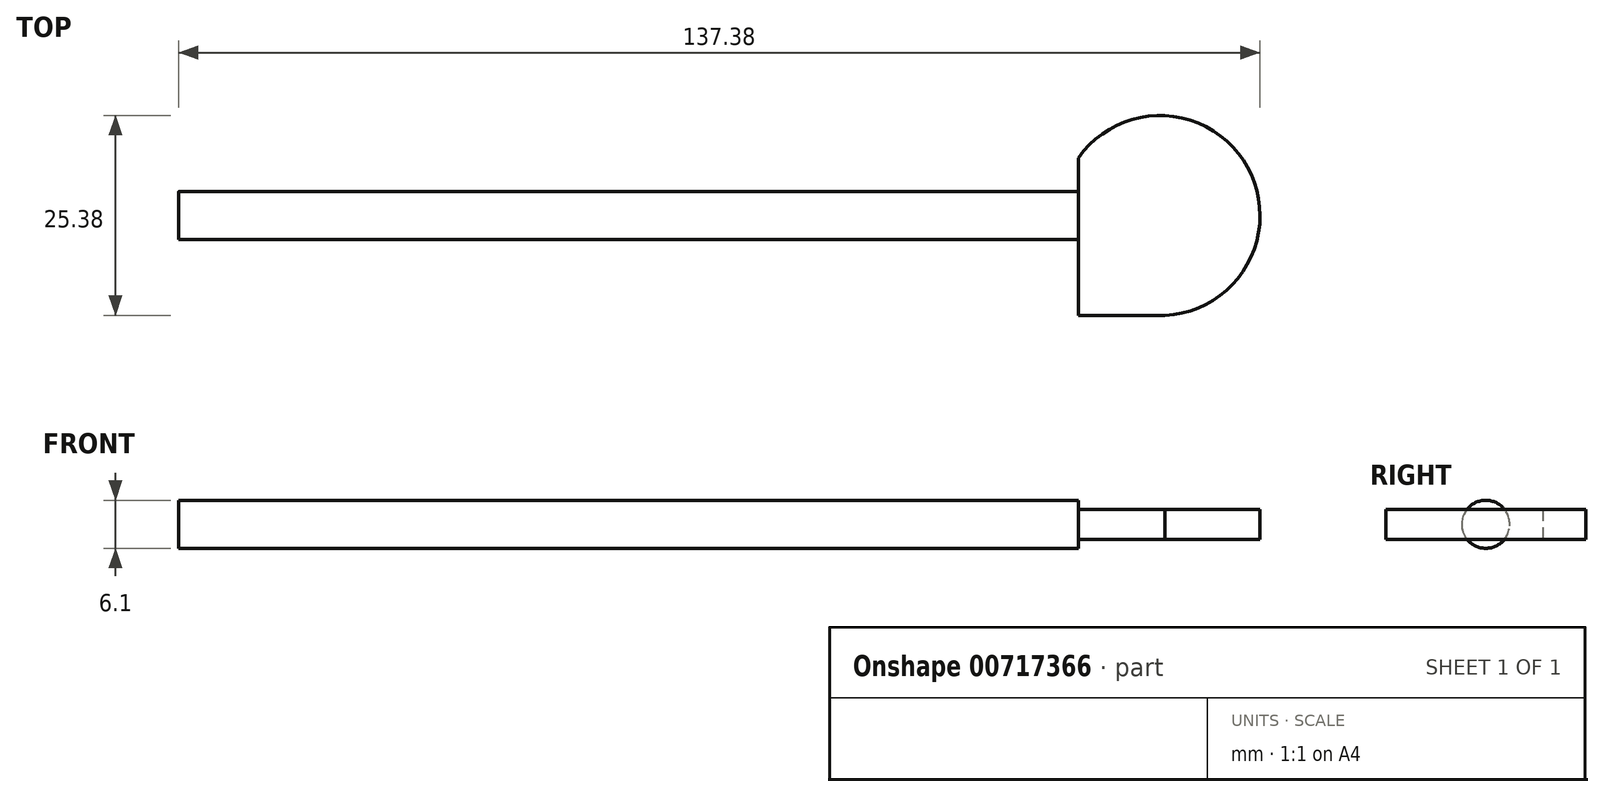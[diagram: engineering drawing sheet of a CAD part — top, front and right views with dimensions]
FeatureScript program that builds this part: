
annotation { "Feature Type Name" : "Feature", "Feature Type Description" : "" }
export const myFeature = defineFeature(function(context is Context, id is Id, definition is map)
    precondition{}
    {
        {
            var Q0;
            Q0=qCreatedBy(makeId("Right.planeOp"),FACE);
            var sketch = newSketch(context, id + "F0", { "sketchPlane" : qUnion([Q0])});
            skCircle(sketch, "E0", {"center": v(0, 0) * mm, "radius": 3.05 * mm});
            skSolve(sketch);
        }
        {
            var Q0;
            Q0=makeQuery(id+"F0.imprint","IMPRINT",FACE,{"disambiguationData":[TD([[makeQuery(id+"F0.imprint","IMPRINT",EDGE,{"derivedFrom":sQuery(id+"F0.wireOp",EDGE,"E0")}),1.0]])]});
            extrude(context, id + "F1", {"entities" : qUnion([Q0]), "depth" : 114.3 * mm, "offsetDistance" : 25.4 * mm});
        }
        {
            var Q0;
            Q0=makeQuery(id+"F1.opExtrude","CAP_FACE",FACE,{"disambiguationData":[OSD([sQuery(id+"F0.wireOp",EDGE,"E0")])],"isStart":false});
            var sketch = newSketch(context, id + "F2", { "sketchPlane" : qUnion([Q0])});
            skLineSegment(sketch, "E1", {"start": v(-0.77, 2.95) * mm, "end": v(0.8, -2.94) * mm, "construction": true});
            skLineSegment(sketch, "E2", {"start": v(-2.81, -1.18) * mm, "end": v(2.81, 1.18) * mm, "construction": true});
            skLineSegment(sketch, "E3.bottom", {"start": v(12.72, -1.9) * mm, "end": v(-12.68, -1.9) * mm});
            skLineSegment(sketch, "E3.top", {"start": v(12.72, 1.91) * mm, "end": v(-12.68, 1.91) * mm});
            skLineSegment(sketch, "E3.left", {"start": v(12.72, -1.9) * mm, "end": v(12.72, 1.91) * mm});
            skLineSegment(sketch, "E3.right", {"start": v(-12.68, -1.9) * mm, "end": v(-12.68, 1.91) * mm});
            skPoint(sketch, "E3.middle", {"position": v(0.02, 0) * mm});
            skSolve(sketch);
        }
        {
            var Q0;
            {var subQ0=sQuery(id+"F2.wireOp",EDGE,"E3.right");Q0=makeQuery(id+"F2.imprint","IMPRINT",FACE,{"disambiguationData":[TD([[makeQuery(id+"F2.imprint","IMPRINT",EDGE,{"derivedFrom":subQ0}),-1.0]])]});}
            var Q1;
            {var subQ0=sQuery(id+"F2.wireOp",EDGE,"E3.bottom");var subQ1=makeQuery(id+"F1.opExtrude","CAP_EDGE",EDGE,{"disambiguationData":[OSD([sQuery(id+"F0.wireOp",EDGE,"E0")])],"isStart":false});var subQ2=makeQuery(id+"F2.imprint","INTERSECT",VERTEX,{"disambiguationData":[OD(0.0)],"derivedFrom":[subQ1,subQ0]});Q1=makeQuery(id+"F2.imprint","IMPRINT",FACE,{"disambiguationData":[TD([[makeQuery(id+"F2.imprint","IMPRINT",EDGE,{"disambiguationData":[TD([[subQ2,-1.0]])],"derivedFrom":subQ0}),-1.0]])]});}
            var Q2;
            {var subQ0=sQuery(id+"F2.wireOp",EDGE,"E3.left");Q2=makeQuery(id+"F2.imprint","IMPRINT",FACE,{"disambiguationData":[TD([[makeQuery(id+"F2.imprint","IMPRINT",EDGE,{"derivedFrom":subQ0}),1.0]])]});}
            extrude(context, id + "F3", {"entities" : qUnion([Q0, Q1, Q2]), "operationType" : NewBodyOperationType.ADD, "depth" : 25.4 * mm, "offsetDistance" : 25.4 * mm});
        }
        {
            var Q0;
            Q0=makeQuery(id+"F3.opExtrude","SWEPT_FACE",FACE,{"disambiguationData":[OSD([sQuery(id+"F2.wireOp",EDGE,"E3.top")])]});
            var sketch = newSketch(context, id + "F4", { "sketchPlane" : qUnion([Q0])});
            skCircle(sketch, "E4", {"center": v(124.68, 0) * mm, "radius": 12.7 * mm});
            skSolve(sketch);
        }
        {
            var Q0;
            {var subQ0=sQuery(id+"F2.wireOp",EDGE,"E3.top");var subQ1=makeQuery(id+"F3.opExtrude","CAP_EDGE",EDGE,{"disambiguationData":[OSD([subQ0])],"isStart":false});Q0=makeQuery(id+"F4.imprint","IMPRINT",FACE,{"disambiguationData":[TD([[makeQuery(id+"F4.imprint","IMPRINT",EDGE,{"derivedFrom":subQ1}),-1.0]])]});}
            var Q1;
            {var subQ0=sQuery(id+"F4.wireOp",EDGE,"E4");var subQ1=sQuery(id+"F2.wireOp",EDGE,"E3.top");var subQ3=sQuery(id+"F2.wireOp",EDGE,"E3.right");var subQ8=makeQuery(id+"F3.opExtrude","SWEPT_EDGE",EDGE,{"disambiguationData":[OSD([subQ1,subQ3])]});var subQ9=makeQuery(id+"F4.imprint","INTERSECT",VERTEX,{"disambiguationData":[OD(0.0)],"derivedFrom":[subQ8,subQ0]});Q1=makeQuery(id+"F4.imprint","IMPRINT",FACE,{"disambiguationData":[TD([[makeQuery(id+"F4.imprint","IMPRINT",EDGE,{"disambiguationData":[TD([[subQ9,1.0]])],"derivedFrom":subQ0}),-1.0]])]});}
            extrude(context, id + "F5", {"entities" : qUnion([Q0, Q1]), "operationType" : NewBodyOperationType.REMOVE, "oppositeDirection" : true, "depth" : 25.4 * mm, "offsetDistance" : 25.4 * mm});
        }
    });
